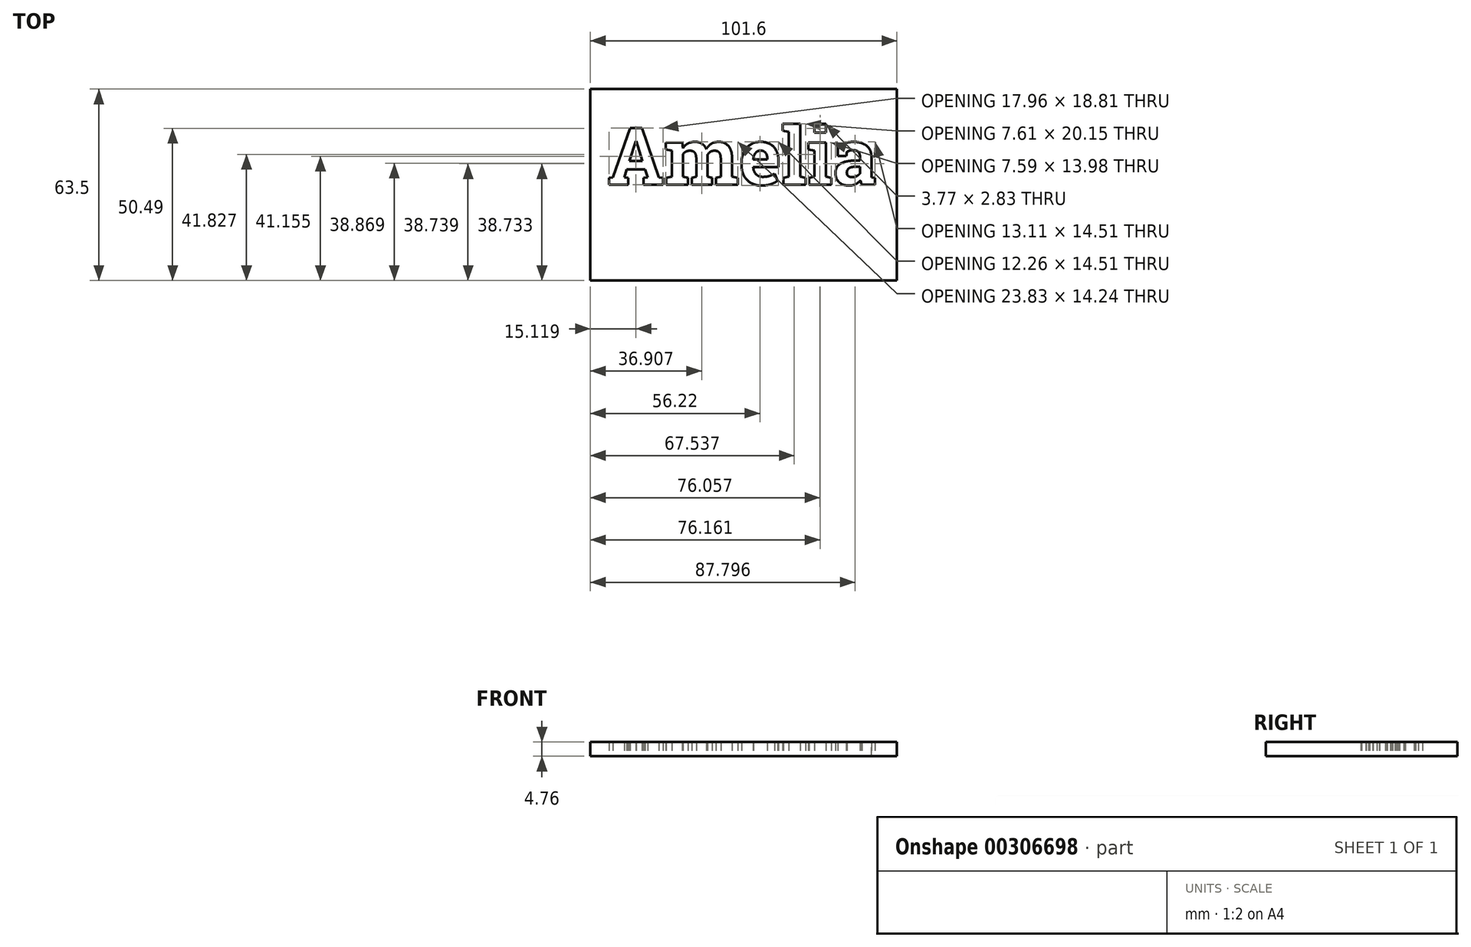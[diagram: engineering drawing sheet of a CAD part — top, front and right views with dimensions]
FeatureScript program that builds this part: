
annotation { "Feature Type Name" : "Feature", "Feature Type Description" : "" }
export const myFeature = defineFeature(function(context is Context, id is Id, definition is map)
    precondition{}
    {
        {
            var Q0;
            Q0=qCreatedBy(makeId("Top.planeOp"),FACE);
            var sketch = newSketch(context, id + "F0", { "sketchPlane" : qUnion([Q0])});
            skLineSegment(sketch, "E0.bottom", {"start": v(-43.67, 27.98) * mm, "end": v(57.93, 27.98) * mm});
            skLineSegment(sketch, "E0.top", {"start": v(-43.67, -35.52) * mm, "end": v(57.93, -35.52) * mm});
            skLineSegment(sketch, "E0.left", {"start": v(-43.67, 27.98) * mm, "end": v(-43.67, -35.52) * mm});
            skLineSegment(sketch, "E0.right", {"start": v(57.93, 27.98) * mm, "end": v(57.93, -35.52) * mm});
            skText(sketch, "E1", { "text": "Amelia", "fontName": "RobotoSlab-Bold.ttf"});
            skPoint(sketch, "E2", {"position": v(7.13, 27.98) * mm});
            const initialGuessF0  = {"E1": [-0.03806, -0.00377, 1, 0, 0.01905]};
            skSetInitialGuess(sketch, initialGuessF0);
            skSolve(sketch);
        }
        {
            var Q0;
            Q0 = qSketchRegion(id + "F0", true);
            var Q1;
            Q1=makeQuery(id+"F0.imprint","IMPRINT",FACE,{"disambiguationData":[TD([[makeQuery(id+"F0.imprint","IMPRINT",EDGE,{"derivedFrom":sQuery(id+"F0.wireOp",EDGE,"E1.sketch_text.stroke-16")}),1.0]])]});
            var Q2;
            Q2=makeQuery(id+"F0.imprint","IMPRINT",FACE,{"disambiguationData":[TD([[makeQuery(id+"F0.imprint","IMPRINT",EDGE,{"derivedFrom":sQuery(id+"F0.wireOp",EDGE,"E1.sketch_text.stroke-80")}),1.0]])]});
            var Q3;
            Q3=makeQuery(id+"F0.imprint","IMPRINT",FACE,{"disambiguationData":[TD([[makeQuery(id+"F0.imprint","IMPRINT",EDGE,{"derivedFrom":sQuery(id+"F0.wireOp",EDGE,"E1.sketch_text.stroke-138")}),1.0]])]});
            extrude(context, id + "F1", {"entities" : qUnion([Q0, Q1, Q2, Q3]), "depth" : 4.76 * mm});
        }
    });
